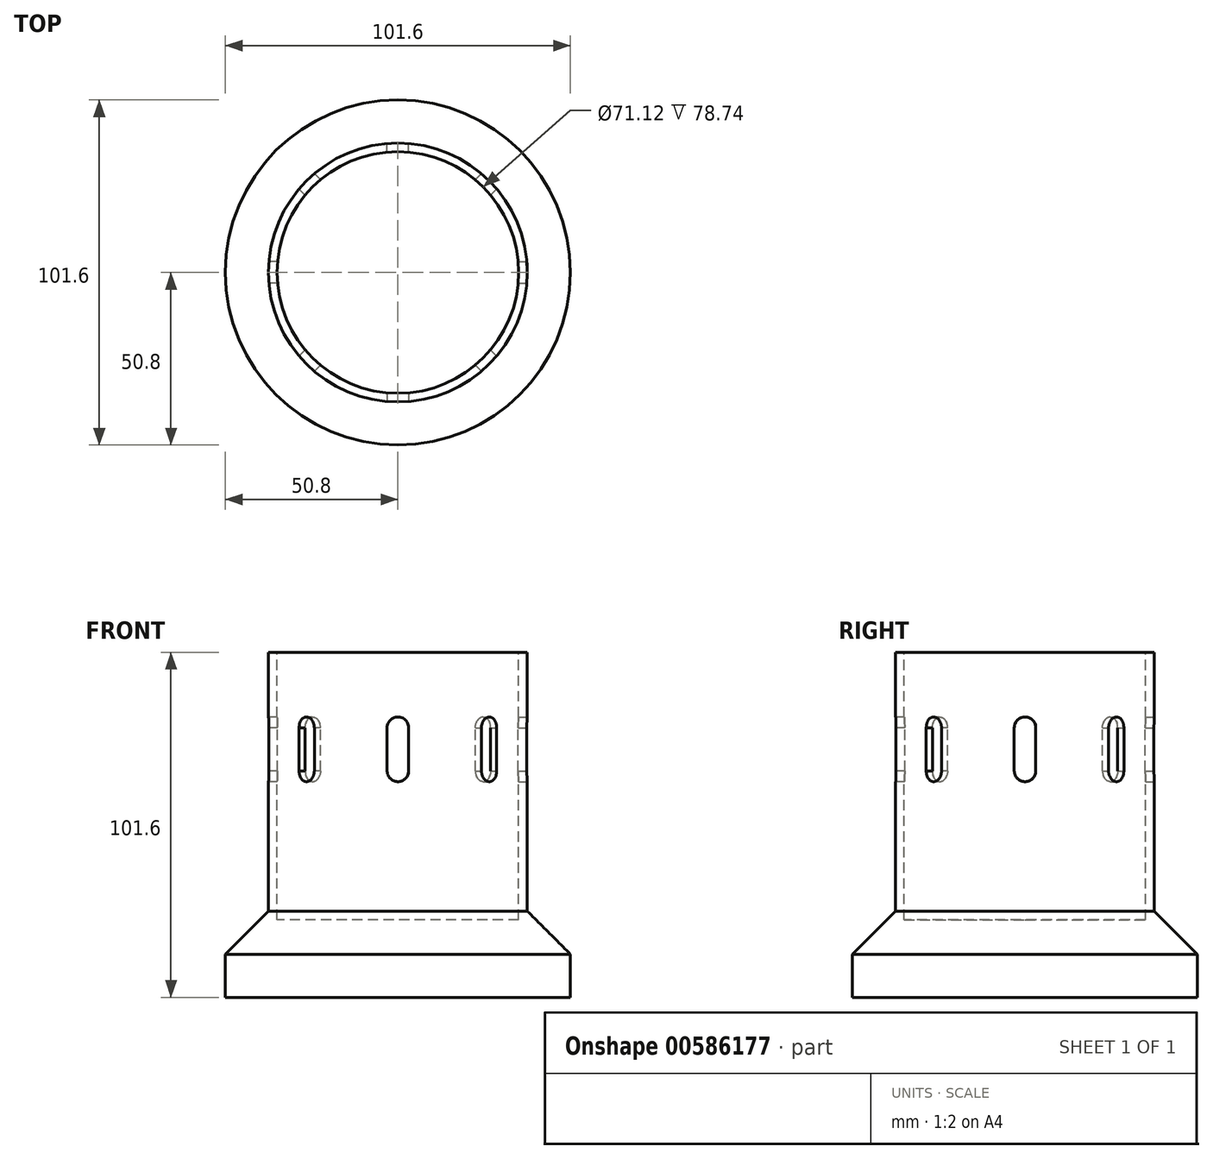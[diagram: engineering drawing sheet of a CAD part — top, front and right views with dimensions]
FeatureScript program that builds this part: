
annotation { "Feature Type Name" : "Feature", "Feature Type Description" : "" }
export const myFeature = defineFeature(function(context is Context, id is Id, definition is map)
    precondition{}
    {
        {
            var Q0;
            Q0=qCreatedBy(makeId("Top.planeOp"),FACE);
            var sketch = newSketch(context, id + "F0", { "sketchPlane" : qUnion([Q0])});
            skCircle(sketch, "E0", {"center": v(0, 0) * mm, "radius": 38.1 * mm});
            skSolve(sketch);
        }
        {
            var Q0;
            Q0 = qSketchRegion(id + "F0", true);
            extrude(context, id + "F1", {"entities" : qUnion([Q0]), "depth" : 101.6 * mm, "offsetDistance" : 25.4 * mm});
        }
        {
            var Q0;
            Q0=makeQuery(id+"F1.opExtrude","CAP_FACE",FACE,{"disambiguationData":[OSD([sQuery(id+"F0.wireOp",EDGE,"E0")])],"isStart":false});
            var sketch = newSketch(context, id + "F2", { "sketchPlane" : qUnion([Q0])});
            skCircle(sketch, "E1", {"center": v(0, 0) * mm, "radius": 35.56 * mm});
            skSolve(sketch);
        }
        {
            var Q0;
            Q0 = qSketchRegion(id + "F2", true);
            extrude(context, id + "F3", {"entities" : qUnion([Q0]), "operationType" : NewBodyOperationType.REMOVE, "oppositeDirection" : true, "depth" : 78.74 * mm, "offsetDistance" : 25.4 * mm});
        }
        {
            var Q0;
            Q0=makeQuery(id+"F1.opExtrude","CAP_FACE",FACE,{"disambiguationData":[OSD([sQuery(id+"F0.wireOp",EDGE,"E0")])],"isStart":false});
            var sketch = newSketch(context, id + "F4", { "sketchPlane" : qUnion([Q0])});
            skLineSegment(sketch, "E2", {"start": v(0, 0) * mm, "end": v(-38.1, 0) * mm});
            skSolve(sketch);
        }
        {
            var Q0;
            Q0=sQuery(id+"F4.wireOp",EDGE,"E2");
            var Q1;
            Q1=sQuery(id+"F4.wireOp",VERTEX,"E2.end");
            cPlane(context, id + "F5", {"entities" : qUnion([Q0, Q1]), "cplaneType" : CPlaneType.LINE_POINT, "offset" : 25.4 * mm, "width" : 152.4 * mm, "height" : 152.4 * mm});
        }
        {
            var Q0;
            Q0=qCreatedBy(id+"F5.planeOp",FACE);
            var sketch = newSketch(context, id + "F6", { "sketchPlane" : qUnion([Q0])});
            skLineSegment(sketch, "E3", {"start": v(0, 0) * mm, "end": v(0, 63.5) * mm});
            skArc(sketch, "E4", {"start": v(3.18, 79.38) * mm, "mid": v(-0.04, 82.55) * mm, "end": v(-3.17, 79.3) * mm});
            skArc(sketch, "E5", {"start": v(-3.17, 66.75) * mm, "mid": v(-0.04, 63.5) * mm, "end": v(3.18, 66.67) * mm});
            skLineSegment(sketch, "E6", {"start": v(3.17, 79.38) * mm, "end": v(3.18, 66.67) * mm});
            skLineSegment(sketch, "E7", {"start": v(-3.17, 66.6) * mm, "end": v(-3.17, 79.3) * mm});
            skSolve(sketch);
        }
        {
            var Q0;
            {var subQ5=sQuery(id+"F6.wireOp",EDGE,"E4");Q0=makeQuery(id+"F6.imprint","IMPRINT",FACE,{"disambiguationData":[TD([[makeQuery(id+"F6.imprint","IMPRINT",EDGE,{"derivedFrom":subQ5}),1.0]])]});}
            extrude(context, id + "F7", {"entities" : qUnion([Q0]), "operationType" : NewBodyOperationType.REMOVE, "oppositeDirection" : true, "depth" : 12.7 * mm, "offsetDistance" : 25.4 * mm});
        }
        {
            var Q0;
            Q0=makeQuery(id+"F7.boolean.opBoolean","COPY",FACE,{"derivedFrom":makeQuery(id+"F7.opExtrude","SWEPT_FACE",FACE,{"disambiguationData":[OSD([sQuery(id+"F6.wireOp",EDGE,"E6")])]})});
            var Q1;
            Q1=makeQuery(id+"F7.boolean.opBoolean","COPY",FACE,{"derivedFrom":makeQuery(id+"F7.opExtrude","SWEPT_FACE",FACE,{"disambiguationData":[OSD([sQuery(id+"F6.wireOp",EDGE,"E5")])]})});
            var Q2;
            Q2=makeQuery(id+"F7.boolean.opBoolean","COPY",FACE,{"derivedFrom":makeQuery(id+"F7.opExtrude","SWEPT_FACE",FACE,{"disambiguationData":[OSD([sQuery(id+"F6.wireOp",EDGE,"E4")])]})});
            var Q3;
            Q3=makeQuery(id+"F7.boolean.opBoolean","COPY",FACE,{"derivedFrom":makeQuery(id+"F7.opExtrude","SWEPT_FACE",FACE,{"disambiguationData":[OSD([sQuery(id+"F6.wireOp",EDGE,"E7")])]})});
            var Q4;
            Q4=makeQuery(id+"F1.opExtrude","CAP_EDGE",EDGE,{"disambiguationData":[OSD([sQuery(id+"F0.wireOp",EDGE,"E0")])],"isStart":true});
            circularPattern(context, id + "F8", {"patternType" : PatternType.FACE, "operationType" : NewBodyOperationType.ADD, "faces" : qUnion([Q0, Q1, Q2, Q3]), "axis" : qUnion([Q4]), "angle" : 360 * degree, "instanceCount" : 8, "equalSpace" : true});
        }
        {
            var Q0;
            Q0=qCreatedBy(makeId("Top.planeOp"),FACE);
            var sketch = newSketch(context, id + "F9", { "sketchPlane" : qUnion([Q0])});
            skCircle(sketch, "E8", {"center": v(0, 0) * mm, "radius": 50.8 * mm});
            skSolve(sketch);
        }
        {
            var Q0;
            Q0=makeQuery(id+"F9.imprint","IMPRINT",FACE,{"disambiguationData":[TD([[makeQuery(id+"F9.imprint","IMPRINT",EDGE,{"derivedFrom":sQuery(id+"F9.wireOp",EDGE,"E8")}),1.0]])]});
            extrude(context, id + "F10", {"entities" : qUnion([Q0]), "operationType" : NewBodyOperationType.ADD, "depth" : 12.7 * mm, "offsetDistance" : 25.4 * mm});
        }
        {
            var Q0;
            Q0=makeQuery(id+"F10.boolean.opBoolean","INTERSECT",EDGE,{"derivedFrom":[makeQuery(id+"F1.opExtrude","SWEPT_FACE",FACE,{"disambiguationData":[OSD([sQuery(id+"F0.wireOp",EDGE,"E0")])]}),makeQuery(id+"F10.opExtrude","CAP_FACE",FACE,{"disambiguationData":[OSD([sQuery(id+"F9.wireOp",EDGE,"E8")])],"isStart":false})]});
            chamfer(context, id + "F11", {"entities" : qUnion([Q0]), "chamferType" : ChamferType.OFFSET_ANGLE, "width" : 12.7 * mm, "oppositeDirection" : false, "angle" : 45 * degree, "tangentPropagation" : true});
        }
    });
